# Revit family: 45-59-020 DN50-400
name_source: partatom
category: Pipe Accessories
units: mm (PartAtom-declared; Revit-internal decimal feet)

## family parameters
Always vertical = No
Cut with Voids When Loaded = No
Part Type = Valve - Breaks Into
Round Connector Dimension = Use Diameter
Shared = No
Work Plane-Based = No

## types (7) — shared parameters
1 = 1 mm  [stored 0.00328084 ft]
5 = 5 mm  [stored 0.0164042 ft]
DN050_PN10/16 = 45-050-59-01614
DN250_PN16 = 45-250-59-016B4
DN300_PN10 = 45-300-59-006B4
DN300_PN16 = 45-300-59-016B4
DN350_PN16 = 45-350-5D-016B4
DN400_PN10 = 45-400-5D-006B4
DN400_PN16 = 45-400-5D-016B4
Description_ = AVK GATE VALVE, FLANGED
Search_table = 45-59-020 DN50-400
URL product pages = https://www.avkvalves.com
zero-valued in all types: Default Elevation

## per-type parameters (varying)
- DN050_PN10/16: Body_FL_L=75 mm; Body_FL_W=57.5 mm; Body_H=121 mm; Body_L=63 mm; Body_T=8 mm  [stored 0.0262467 ft]; Body_W=43 mm  [stored 0.141076 ft]; Body_rib_L=40 mm  [stored 0.131234 ft]; Body_wedge_dim=10 mm  [stored 0.0328084 ft]; Bonnet_H=63 mm; Bonnet_dim=82 mm; Bonnet_dim1=106.2 mm; Bonnet_dim2=27.09 mm  [stored 0.088878 ft]; Bonnet_lift1=77.9 mm; Bonnet_lift2=69.7 mm; Bonnet_lift3=10.54 mm; Bore_R=25 mm  [stored 0.082021 ft]; DN=50 mm; FL_OD=82.5 mm; FL_T=16 mm  [stored 0.0524934 ft]; H=293 mm; H3=383 mm; L=169 mm; Logo_H.=24.2 mm; Raised_R=3 mm  [stored 0.00984252 ft]; Raised_R1=64.35 mm; Rib1_H=25 mm  [stored 0.082021 ft]; Rib1_L=50 mm; Rib1_R=15 mm  [stored 0.0492126 ft]; Rib1_W=25 mm  [stored 0.082021 ft]; Rib2_H=25 mm  [stored 0.082021 ft]; Rib2_L=50 mm; Rib2_W=25 mm  [stored 0.082021 ft]; Rib3_H=25 mm  [stored 0.082021 ft]; Rib3_L=50 mm; Rib3_W=25 mm  [stored 0.082021 ft]; Rib_T=4 mm  [stored 0.0131234 ft]; Stem_cap1=17.2 mm; Stem_cap2=15.05 mm  [stored 0.0493766 ft]; Stem_cap_H1=55 mm; Stem_cap_H2=49 mm; Stem_cap_H3=70 mm; Stem_cap_dim1=23.89 mm; W=82.5 mm; stem_R=10.54 mm
- DN250_PN16: Body_FL_L=190 mm; Body_FL_W=110 mm; Body_H=300 mm; Body_L=160 mm; Body_T=19 mm  [stored 0.062336 ft]; Body_W=90 mm; Body_rib_L=90 mm; Body_wedge_dim=50 mm; Bonnet_H=160 mm; Bonnet_dim=223 mm; Bonnet_dim1=198 mm; Bonnet_dim2=56.7 mm; Bonnet_lift1=211.85 mm; Bonnet_lift2=189.55 mm; Bonnet_lift3=22.05 mm  [stored 0.0723425 ft]; Bore_R=125 mm; DN=250 mm; FL_OD=200 mm; FL_T=28 mm  [stored 0.0918635 ft]; H=628 mm; H3=832 mm; L=330 mm; Logo_H.=60 mm; Raised_R=3 mm  [stored 0.00984252 ft]; Raised_R1=156 mm; Rib1_H=25 mm  [stored 0.082021 ft]; Rib1_L=75 mm; Rib1_R=30 mm  [stored 0.0984252 ft]; Rib1_W=32.5 mm  [stored 0.106627 ft]; Rib2_H=25 mm  [stored 0.082021 ft]; Rib2_L=75 mm; Rib2_W=32.5 mm  [stored 0.106627 ft]; Rib3_H=25 mm  [stored 0.082021 ft]; Rib3_L=75 mm; Rib3_W=32.5 mm  [stored 0.106627 ft]; Rib_T=6 mm  [stored 0.019685 ft]; Stem_cap1=36 mm  [stored 0.11811 ft]; Stem_cap2=31.5 mm  [stored 0.103346 ft]; Stem_cap_H1=60 mm; Stem_cap_H2=49 mm; Stem_cap_H3=70 mm; Stem_cap_dim1=50 mm; W=203.5 mm; stem_R=22.05 mm  [stored 0.0723425 ft]
- DN300_PN10: Body_FL_L=241.5 mm; Body_FL_W=142 mm; Body_H=372 mm; Body_L=213 mm; Body_T=19 mm  [stored 0.062336 ft]; Body_W=114 mm; Body_rib_L=110 mm; Body_wedge_dim=60 mm; Bonnet_H=213 mm; Bonnet_dim=245 mm; Bonnet_dim1=245.7 mm; Bonnet_dim2=71.82 mm; Bonnet_lift1=232.75 mm; Bonnet_lift2=208.25 mm; Bonnet_lift3=27.93 mm  [stored 0.0916339 ft]; Bore_R=150 mm; DN=300 mm; FL_OD=241.5 mm; FL_T=28 mm  [stored 0.0918635 ft]; H=701 mm; H3=943 mm; L=356 mm; Logo_H.=74.4 mm; Raised_R=3 mm  [stored 0.00984252 ft]; Raised_R1=188.37 mm; Rib1_H=125 mm; Rib1_L=231 mm; Rib1_R=40 mm  [stored 0.131234 ft]; Rib1_W=150 mm; Rib2_H=280 mm; Rib2_L=231 mm; Rib2_W=150 mm; Rib3_H=35 mm  [stored 0.114829 ft]; Rib3_L=231 mm; Rib3_W=150 mm; Rib_T=8 mm  [stored 0.0262467 ft]; Stem_cap1=45.6 mm  [stored 0.149606 ft]; Stem_cap2=39.9 mm  [stored 0.130906 ft]; Stem_cap_H1=60 mm; Stem_cap_H2=49 mm; Stem_cap_H3=70 mm; Stem_cap_dim1=63.33 mm; W=241.5 mm; stem_R=27.93 mm  [stored 0.0916339 ft]
- DN300_PN16: Body_FL_L=241.5 mm; Body_FL_W=142 mm; Body_H=372 mm; Body_L=213 mm; Body_T=19 mm  [stored 0.062336 ft]; Body_W=114 mm; Body_rib_L=110 mm; Body_wedge_dim=60.02 mm; Bonnet_H=213 mm; Bonnet_dim=245 mm; Bonnet_dim1=245.7 mm; Bonnet_dim2=71.82 mm; Bonnet_lift1=232.75 mm; Bonnet_lift2=208.25 mm; Bonnet_lift3=27.93 mm  [stored 0.0916339 ft]; Bore_R=150.05 mm; DN=300.1 mm; FL_OD=241.5 mm; FL_T=28 mm  [stored 0.0918635 ft]; H=701 mm; H3=944 mm; L=356 mm; Logo_H.=74.4 mm; Raised_R=3 mm  [stored 0.00984252 ft]; Raised_R1=188.37 mm; Rib1_H=125 mm; Rib1_L=231 mm; Rib1_R=40 mm  [stored 0.131234 ft]; Rib1_W=150 mm; Rib2_H=280 mm; Rib2_L=231 mm; Rib2_W=150 mm; Rib3_H=35 mm  [stored 0.114829 ft]; Rib3_L=231 mm; Rib3_W=150 mm; Rib_T=8 mm  [stored 0.0262467 ft]; Stem_cap1=45.6 mm  [stored 0.149606 ft]; Stem_cap2=39.9 mm  [stored 0.130906 ft]; Stem_cap_H1=60 mm; Stem_cap_H2=49 mm; Stem_cap_H3=70 mm; Stem_cap_dim1=63.33 mm; W=241.5 mm; stem_R=27.93 mm  [stored 0.0916339 ft]
- DN350_PN16: Body_FL_L=293 mm; Body_FL_W=150 mm; Body_H=450 mm; Body_L=242.5 mm; Body_T=19 mm  [stored 0.062336 ft]; Body_W=122.5 mm; Body_rib_L=125 mm; Body_wedge_dim=70 mm; Bonnet_H=242 mm; Bonnet_dim=304 mm; Bonnet_dim1=304.65 mm; Bonnet_dim2=77.18 mm; Bonnet_lift1=288.8 mm; Bonnet_lift2=258.4 mm; Bonnet_lift3=30.01 mm; Bore_R=175 mm; DN=350 mm; FL_OD=266.5 mm; FL_T=33 mm  [stored 0.108268 ft]; H=891 mm; H3=1158 mm; L=381 mm; Logo_H.=90 mm; Raised_R=4 mm  [stored 0.0131234 ft]; Raised_R1=207.87 mm; Rib1_H=150 mm; Rib1_L=250 mm; Rib1_R=45 mm  [stored 0.147638 ft]; Rib1_W=145 mm; Rib2_H=310 mm; Rib2_L=250 mm; Rib2_W=145 mm; Rib3_H=35 mm  [stored 0.114829 ft]; Rib3_L=250 mm; Rib3_W=145 mm; Rib_T=9 mm  [stored 0.0295276 ft]; Stem_cap1=49 mm; Stem_cap2=42.88 mm; Stem_cap_H1=96 mm; Stem_cap_H2=80.5 mm; Stem_cap_H3=115 mm; Stem_cap_dim1=68.06 mm; W=266.5 mm; stem_R=30.01 mm
- DN400_PN10: Body_FL_L=283 mm; Body_FL_W=157 mm; Body_H=523 mm; Body_L=250 mm; Body_T=22 mm  [stored 0.0721785 ft]; Body_W=131 mm; Body_rib_L=140 mm; Body_wedge_dim=80 mm; Bonnet_H=220 mm; Bonnet_dim=265 mm; Bonnet_dim1=297 mm; Bonnet_dim2=82.53 mm; Bonnet_lift1=251.75 mm; Bonnet_lift2=225.25 mm; Bonnet_lift3=32.1 mm; Bore_R=200 mm; DN=400 mm; FL_OD=298.5 mm; FL_T=37 mm  [stored 0.121391 ft]; H=893 mm; H3=1192 mm; L=406 mm; Logo_H.=104.6 mm; Raised_R=4 mm  [stored 0.0131234 ft]; Raised_R1=232.83 mm; Rib1_H=185 mm; Rib1_L=290 mm; Rib1_R=50 mm; Rib1_W=138 mm; Rib2_H=339 mm; Rib2_L=290 mm; Rib2_W=138 mm; Rib3_H=493 mm; Rib3_L=290 mm; Rib3_W=138 mm; Rib_T=9 mm  [stored 0.0295276 ft]; Stem_cap1=52.4 mm; Stem_cap2=45.85 mm  [stored 0.150427 ft]; Stem_cap_H1=80 mm; Stem_cap_H2=33.6 mm  [stored 0.110236 ft]; Stem_cap_H3=48 mm; Stem_cap_dim1=72.78 mm; W=298.5 mm; stem_R=32.1 mm
- DN400_PN16: Body_FL_L=283 mm; Body_FL_W=157 mm; Body_H=523 mm; Body_L=250 mm; Body_T=22 mm  [stored 0.0721785 ft]; Body_W=131 mm; Body_rib_L=140 mm; Body_wedge_dim=80.02 mm; Bonnet_H=220 mm; Bonnet_dim=265 mm; Bonnet_dim1=297 mm; Bonnet_dim2=82.53 mm; Bonnet_lift1=251.75 mm; Bonnet_lift2=225.25 mm; Bonnet_lift3=32.1 mm; Bore_R=200.05 mm; DN=400.1 mm; FL_OD=298.5 mm; FL_T=37 mm  [stored 0.121391 ft]; H=893 mm; H3=1192 mm; L=406 mm; Logo_H.=104.6 mm; Raised_R=4 mm  [stored 0.0131234 ft]; Raised_R1=232.83 mm; Rib1_H=185 mm; Rib1_L=290 mm; Rib1_R=50 mm; Rib1_W=138 mm; Rib2_H=339 mm; Rib2_L=290 mm; Rib2_W=138 mm; Rib3_H=493 mm; Rib3_L=290 mm; Rib3_W=138 mm; Rib_T=10 mm  [stored 0.0328084 ft]; Stem_cap1=52.4 mm; Stem_cap2=45.85 mm  [stored 0.150427 ft]; Stem_cap_H1=80 mm; Stem_cap_H2=33.6 mm  [stored 0.110236 ft]; Stem_cap_H3=48 mm; Stem_cap_dim1=72.78 mm; W=298.5 mm; stem_R=32.1 mm

note: [stored X ft] marks values corroborated as IEEE doubles in the binary element streams (Revit-internal decimal feet)

## geometry (parser evidence)
native form markers: Sweep x6
no freeform markers — native parametric forms only
